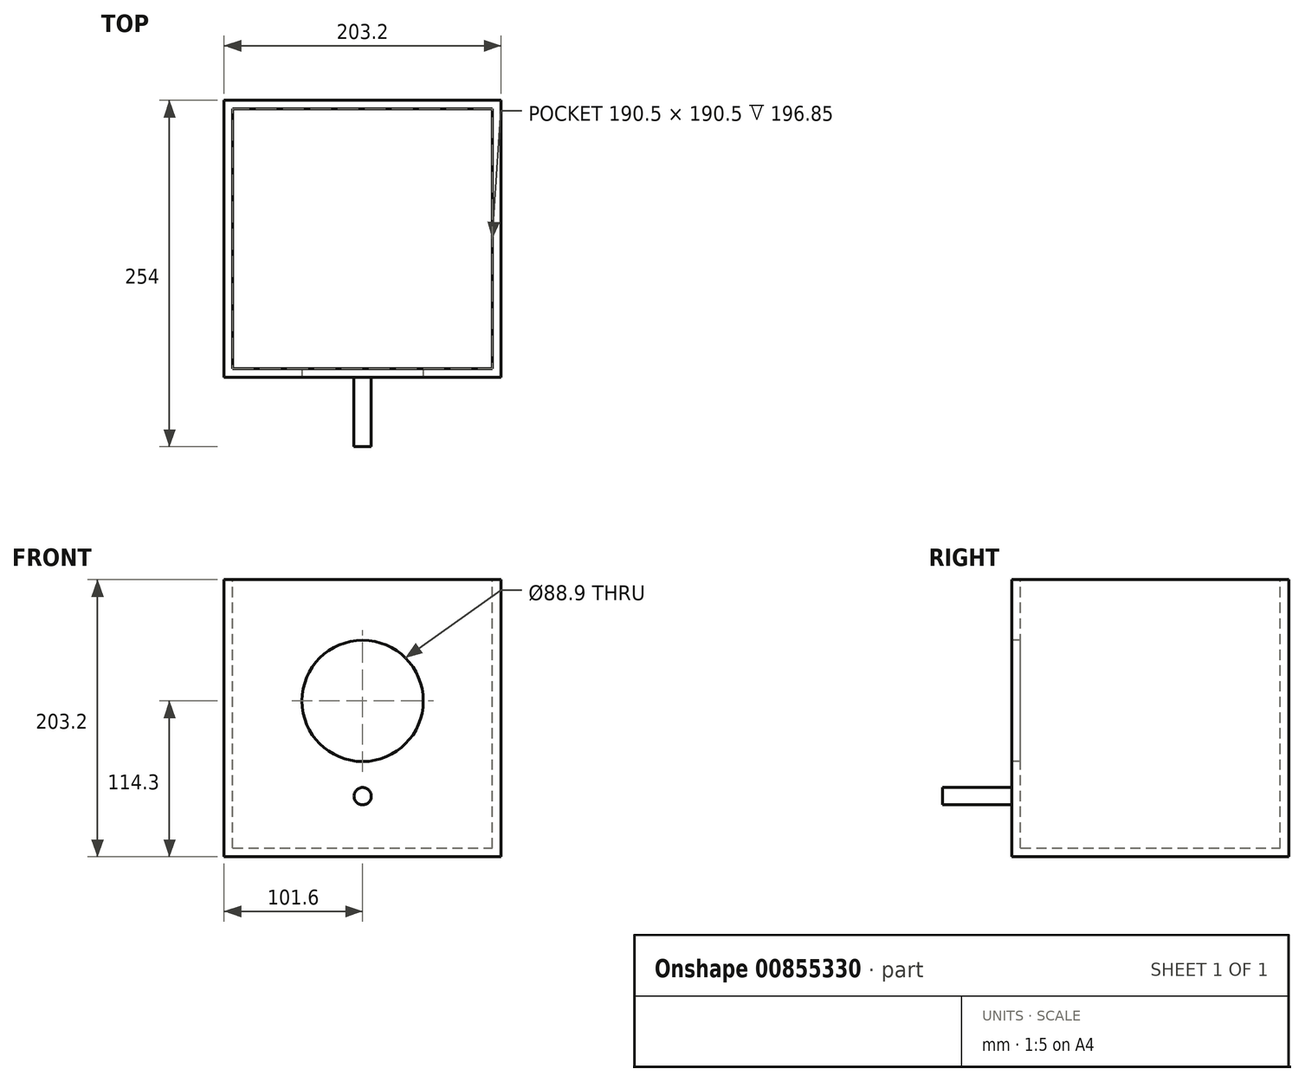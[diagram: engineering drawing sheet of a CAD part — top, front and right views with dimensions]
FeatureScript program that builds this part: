
annotation { "Feature Type Name" : "Feature", "Feature Type Description" : "" }
export const myFeature = defineFeature(function(context is Context, id is Id, definition is map)
    precondition{}
    {
        {
            var Q0;
            Q0=qCreatedBy(makeId("Front.planeOp"),FACE);
            var sketch = newSketch(context, id + "F0", { "sketchPlane" : qUnion([Q0])});
            skLineSegment(sketch, "E0.bottom", {"start": v(0, 0) * mm, "end": v(203.2, 0) * mm});
            skLineSegment(sketch, "E0.top", {"start": v(0, 203.2) * mm, "end": v(203.2, 203.2) * mm});
            skLineSegment(sketch, "E0.left", {"start": v(0, 0) * mm, "end": v(0, 203.2) * mm});
            skLineSegment(sketch, "E0.right", {"start": v(203.2, 0) * mm, "end": v(203.2, 203.2) * mm});
            skSolve(sketch);
        }
        {
            var Q0;
            Q0=makeQuery(id+"F0.imprint","IMPRINT",FACE,{"disambiguationData":[TD([[makeQuery(id+"F0.imprint","IMPRINT",EDGE,{"derivedFrom":sQuery(id+"F0.wireOp",EDGE,"E0.bottom")}),1.0]])]});
            extrude(context, id + "F1", {"entities" : qUnion([Q0]), "depth" : 203.2 * mm, "offsetDistance" : 25.4 * mm});
        }
        {
            var Q0;
            Q0=makeQuery(id+"F1.opExtrude","SWEPT_FACE",FACE,{"disambiguationData":[OSD([sQuery(id+"F0.wireOp",EDGE,"E0.top")])]});
            var Q1;
            Q1=makeQuery(id+"F1.opExtrude","SWEPT_BODY",BODY,{"disambiguationData":[OSD([sQuery(id+"F0.wireOp",EDGE,"E0.bottom"),sQuery(id+"F0.wireOp",EDGE,"E0.top"),sQuery(id+"F0.wireOp",EDGE,"E0.left"),sQuery(id+"F0.wireOp",EDGE,"E0.right")])]});
            shell(context, id + "F2", {"entities" : qUnion([Q0]), "parts" : qUnion([Q1]), "thickness" : 6.35 * mm});
        }
        {
            var Q0;
            Q0=makeQuery(id+"F1.opExtrude","CAP_FACE",FACE,{"disambiguationData":[OSD([sQuery(id+"F0.wireOp",EDGE,"E0.bottom"),sQuery(id+"F0.wireOp",EDGE,"E0.top"),sQuery(id+"F0.wireOp",EDGE,"E0.left"),sQuery(id+"F0.wireOp",EDGE,"E0.right")])],"isStart":false});
            var sketch = newSketch(context, id + "F3", { "sketchPlane" : qUnion([Q0])});
            skCircle(sketch, "E1", {"center": v(101.6, 114.3) * mm, "radius": 44.45 * mm});
            skSolve(sketch);
        }
        {
            var Q0;
            Q0=makeQuery(id+"F3.imprint","IMPRINT",FACE,{"disambiguationData":[TD([[makeQuery(id+"F3.imprint","IMPRINT",EDGE,{"derivedFrom":sQuery(id+"F3.wireOp",EDGE,"E1")}),1.0]])]});
            extrude(context, id + "F4", {"entities" : qUnion([Q0]), "operationType" : NewBodyOperationType.REMOVE, "oppositeDirection" : true, "depth" : 6.35 * mm, "offsetDistance" : 25.4 * mm});
        }
        {
            var Q0;
            Q0=makeQuery(id+"F1.opExtrude","CAP_FACE",FACE,{"disambiguationData":[OSD([sQuery(id+"F0.wireOp",EDGE,"E0.bottom"),sQuery(id+"F0.wireOp",EDGE,"E0.top"),sQuery(id+"F0.wireOp",EDGE,"E0.left"),sQuery(id+"F0.wireOp",EDGE,"E0.right")])],"isStart":false});
            var sketch = newSketch(context, id + "F5", { "sketchPlane" : qUnion([Q0])});
            skCircle(sketch, "E2", {"center": v(101.6, 44.45) * mm, "radius": 6.35 * mm});
            skSolve(sketch);
        }
        {
            var Q0;
            Q0=makeQuery(id+"F5.imprint","IMPRINT",FACE,{"disambiguationData":[TD([[makeQuery(id+"F5.imprint","IMPRINT",EDGE,{"derivedFrom":sQuery(id+"F5.wireOp",EDGE,"E2")}),1.0]])]});
            var Q1;
            Q1=sQuery(id+"F5.wireOp",EDGE,"E2");
            extrude(context, id + "F6", {"entities" : qUnion([Q0]), "surfaceEntities" : qUnion([Q1]), "depth" : 50.8 * mm, "offsetDistance" : 25.4 * mm});
        }
    });
